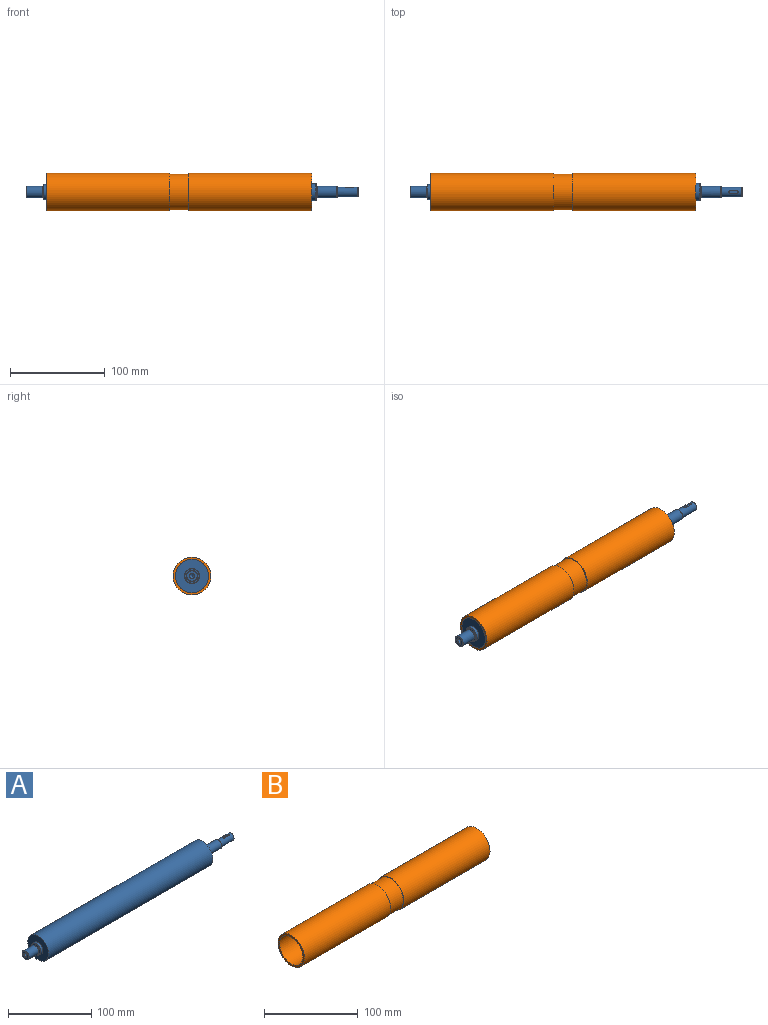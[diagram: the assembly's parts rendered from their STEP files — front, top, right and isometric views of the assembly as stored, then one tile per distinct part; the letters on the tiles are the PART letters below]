
ASSEMBLY  parts=2 mates=1
PART A: 33 faces, bbox 351x35x35 mm
  f0: plane 12x12mm, normal (1,0,0), area 34.6mm2, adj f1,f16
  f1: cylinder r=6mm len=16.5mm, axis (1,0,0), area 622mm2, adj f0,f31
  f2: plane 11x11mm, normal (-1,0,0), area 66.8mm2, adj f31,f32
  f3: plane 9x9mm, normal (1,0,0), area 49.1mm2, adj f29,f30
  f4: cylinder r=5mm len=21.5mm, axis (1,0,0), area 647mm2, adj f5,f21,f22,f23,f24,f30
  f5: plane 11x11mm, normal (1,0,0), area 16.5mm2, adj f4,f27
  f6: cylinder r=6mm len=20.5mm, axis (1,0,0), area 772.8mm2, adj f7,f27
  f7: plane 12x12mm, normal (-1,0,0), area 34.6mm2, adj f6,f8
  f8: cylinder r=5mm len=10mm, axis (1,0,0), area 31.4mm2, adj f7,f9
  f9: plane 17x17mm, normal (1,0,0), area 148.4mm2, adj f8,f26
  f10: cylinder r=9mm len=18mm, axis (1,0,0), area 254.5mm2, adj f11,f26
  f11: plane 35x35mm, normal (1,0,0), area 707.6mm2, adj f10,f12
  f12: cylinder r=17.5mm len=280mm, axis (1,0,0), area 30787.6mm2, adj f11,f13
  f13: plane 35x35mm, normal (-1,0,0), area 761.1mm2, adj f12,f14
  f14: cylinder r=8mm len=16mm, axis (1,0,0), area 175.9mm2, adj f13,f28
  f15: plane 15x15mm, normal (-1,0,0), area 98.2mm2, adj f16,f28
  f16: cylinder r=5mm len=10mm, axis (1,0,0), area 31.4mm2, adj f0,f15
  f17: cone r=0mm half-angle=59deg, axis (-1,0,0), area 22.9mm2, adj f18
  f18: cylinder r=2.5mm len=19.5mm, axis (-1,0,0), area 306.3mm2, adj f17,f32
  f19: cone r=0mm half-angle=59deg, axis (1,0,0), area 10mm2, adj f20
  f20: cylinder r=1.65mm len=9.5mm, axis (1,0,0), area 98.5mm2, adj f19,f29
  f21: plane 7x1.67mm, normal (0,-1,0), area 11.7mm2, adj f4,f22,f24,f25
  f22: cylinder r=1.5mm len=3mm, axis (0,0,-1), area 8.4mm2, adj f4,f21,f23,f25
  f23: plane 7x1.67mm, normal (0,1,0), area 11.7mm2, adj f4,f22,f24,f25
  f24: cylinder r=1.5mm len=3mm, axis (0,0,-1), area 8.4mm2, adj f4,f21,f23,f25
  f25: plane 10x3mm, normal (0,0,1), area 28.1mm2, adj f21,f22,f23,f24
  f26: cone r=8.5mm half-angle=45deg, axis (-1,0,0), area 38.9mm2, adj f9,f10
  f27: cone r=5.5mm half-angle=45deg, axis (-1,0,0), area 25.5mm2, adj f5,f6
  f28: cone r=8mm half-angle=45deg, axis (1,0,0), area 34.4mm2, adj f14,f15
  f29: cone r=1.65mm half-angle=45deg, axis (1,0,0), area 8.4mm2, adj f3,f20
  f30: cone r=4.5mm half-angle=45deg, axis (-1,0,0), area 21.1mm2, adj f3,f4
  f31: cone r=6mm half-angle=45deg, axis (1,0,0), area 25.5mm2, adj f1,f2
  f32: cone r=2.5mm half-angle=45deg, axis (-1,0,0), area 12.2mm2, adj f2,f18
PART B: 8 faces, bbox 280x40x40 mm
  f0: plane 40x40mm, normal (-1,0,0), area 294.5mm2, adj f1,f7
  f1: cylinder r=17.5mm len=280mm, axis (-1,0,0), area 30787.6mm2, adj f0,f2
  f2: plane 40x40mm, normal (1,0,0), area 294.5mm2, adj f1,f3
  f3: cylinder r=20mm len=130mm, axis (-1,0,0), area 16336.3mm2, adj f2,f4
  f4: plane 40x40mm, normal (-1,0,0), area 122.5mm2, adj f3,f5
  f5: cylinder r=19mm len=38mm, axis (-1,0,0), area 2387.6mm2, adj f4,f6
  f6: plane 40x40mm, normal (1,0,0), area 122.5mm2, adj f5,f7
  f7: cylinder r=20mm len=130mm, axis (-1,0,0), area 16336.3mm2, adj f0,f6
PLACE A t=(-20.43,52.44,-31.36)mm
PLACE B t=(1.57,52.44,-31.36)mm
MATE fastened B.f1 <-> A.f1  axis (-1,0,0) through (1.57,52.44,-31.36)mm
